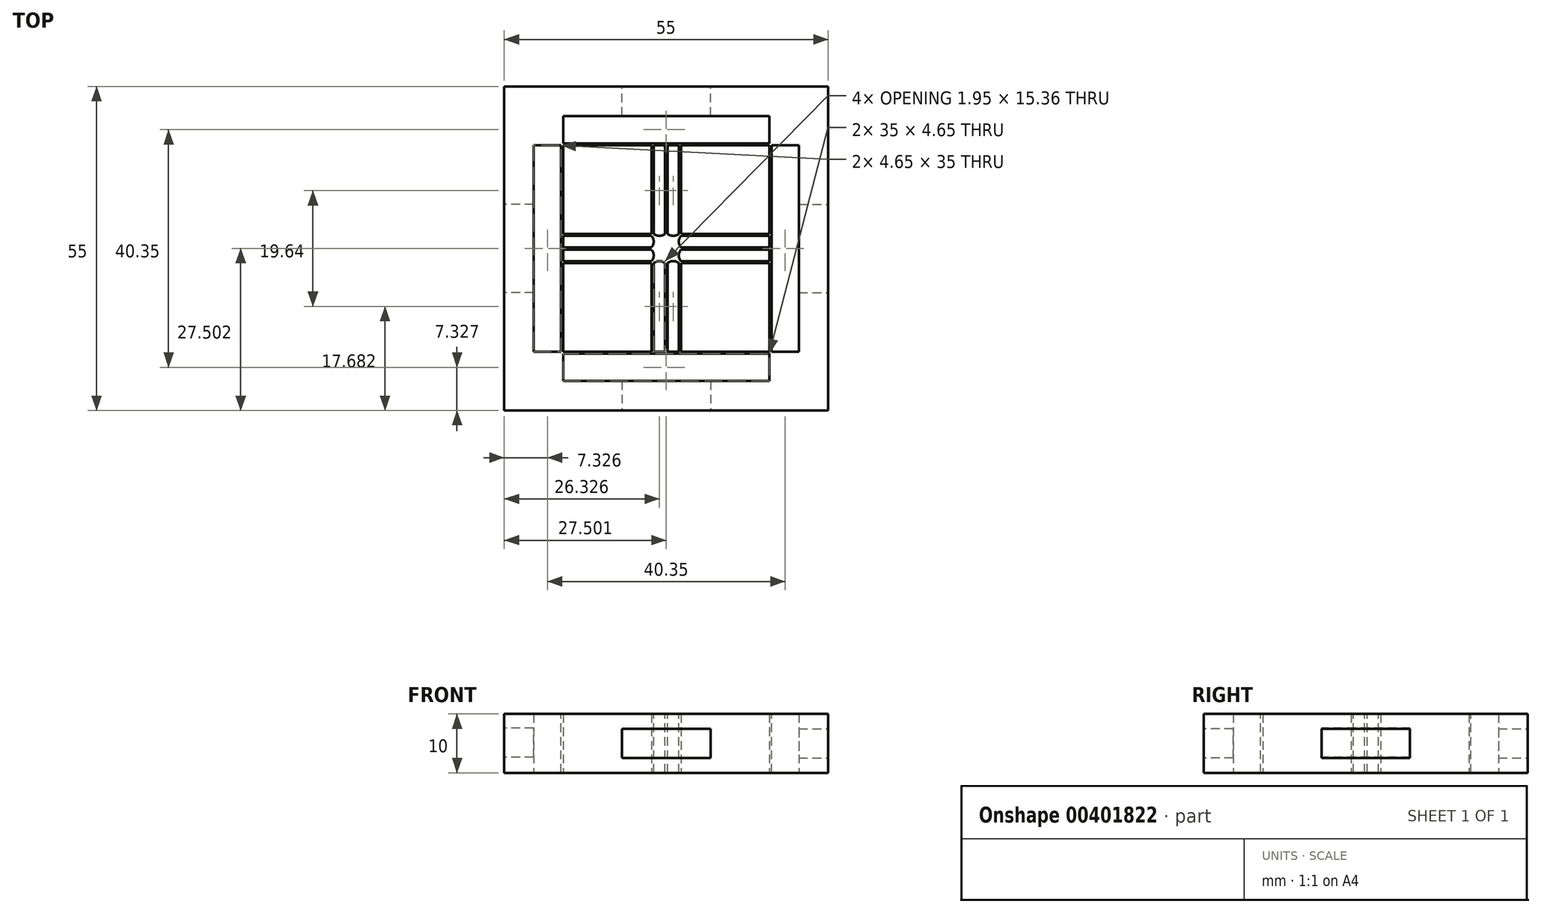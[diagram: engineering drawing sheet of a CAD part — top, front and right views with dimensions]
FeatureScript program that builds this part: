
annotation { "Feature Type Name" : "Feature", "Feature Type Description" : "" }
export const myFeature = defineFeature(function(context is Context, id is Id, definition is map)
    precondition{}
    {
        {
            var Q0;
            Q0=qCreatedBy(makeId("Top.planeOp"),FACE);
            var sketch = newSketch(context, id + "F0", { "sketchPlane" : qUnion([Q0])});
            skLineSegment(sketch, "E0.bottom", {"start": v(-73.72, 37.36) * mm, "end": v(-18.72, 37.36) * mm});
            skLineSegment(sketch, "E0.top", {"start": v(-73.72, -17.64) * mm, "end": v(-18.72, -17.64) * mm});
            skLineSegment(sketch, "E0.left", {"start": v(-73.72, 37.36) * mm, "end": v(-73.72, -17.64) * mm});
            skLineSegment(sketch, "E0.right", {"start": v(-18.72, 37.36) * mm, "end": v(-18.72, -17.64) * mm});
            skSolve(sketch);
        }
        {
            var Q0;
            Q0=makeQuery(id+"F0.imprint","IMPRINT",FACE,{"disambiguationData":[TD([[makeQuery(id+"F0.imprint","IMPRINT",EDGE,{"derivedFrom":sQuery(id+"F0.wireOp",EDGE,"E0.bottom")}),-1.0]])]});
            var sketch = newSketch(context, id + "F1", { "sketchPlane" : qUnion([Q0])});
            skLineSegment(sketch, "E1.bottom", {"start": v(-63.72, 32.36) * mm, "end": v(-28.72, 32.36) * mm});
            skLineSegment(sketch, "E1.top", {"start": v(-63.72, 28.36) * mm, "end": v(-28.72, 28.36) * mm});
            skLineSegment(sketch, "E1.left", {"start": v(-63.72, 32.36) * mm, "end": v(-63.72, 28.36) * mm});
            skLineSegment(sketch, "E1.right", {"start": v(-28.72, 32.36) * mm, "end": v(-28.72, 28.36) * mm});
            skLineSegment(sketch, "E2.bottom", {"start": v(-64.72, 27.36) * mm, "end": v(-68.72, 27.36) * mm});
            skLineSegment(sketch, "E2.top", {"start": v(-64.72, -7.64) * mm, "end": v(-68.72, -7.64) * mm});
            skLineSegment(sketch, "E2.left", {"start": v(-64.72, 27.36) * mm, "end": v(-64.72, -7.64) * mm});
            skLineSegment(sketch, "E2.right", {"start": v(-68.72, 27.36) * mm, "end": v(-68.72, -7.64) * mm});
            skLineSegment(sketch, "E3.bottom", {"start": v(-23.72, 27.36) * mm, "end": v(-27.72, 27.36) * mm});
            skLineSegment(sketch, "E3.top", {"start": v(-23.72, -7.64) * mm, "end": v(-27.72, -7.64) * mm});
            skLineSegment(sketch, "E3.left", {"start": v(-23.72, 27.36) * mm, "end": v(-23.72, -7.64) * mm});
            skLineSegment(sketch, "E3.right", {"start": v(-27.72, 27.36) * mm, "end": v(-27.72, -7.64) * mm});
            skLineSegment(sketch, "E4.bottom", {"start": v(-63.72, -8.64) * mm, "end": v(-28.72, -8.64) * mm});
            skLineSegment(sketch, "E4.top", {"start": v(-63.72, -12.64) * mm, "end": v(-28.72, -12.64) * mm});
            skLineSegment(sketch, "E4.left", {"start": v(-63.72, -8.64) * mm, "end": v(-63.72, -12.64) * mm});
            skLineSegment(sketch, "E4.right", {"start": v(-28.72, -8.64) * mm, "end": v(-28.72, -12.64) * mm});
            skLineSegment(sketch, "E5.bottom", {"start": v(-63.72, 27.36) * mm, "end": v(-48.72, 27.36) * mm});
            skLineSegment(sketch, "E5.top", {"start": v(-63.72, 12.36) * mm, "end": v(-48.72, 12.36) * mm});
            skLineSegment(sketch, "E5.left", {"start": v(-63.72, 27.36) * mm, "end": v(-63.72, 12.36) * mm});
            skLineSegment(sketch, "E5.right", {"start": v(-48.72, 27.36) * mm, "end": v(-48.72, 12.36) * mm});
            skLineSegment(sketch, "E6.bottom", {"start": v(-43.72, 27.36) * mm, "end": v(-28.72, 27.36) * mm});
            skLineSegment(sketch, "E6.top", {"start": v(-43.72, 12.36) * mm, "end": v(-28.72, 12.36) * mm});
            skLineSegment(sketch, "E6.left", {"start": v(-43.72, 27.36) * mm, "end": v(-43.72, 12.36) * mm});
            skLineSegment(sketch, "E6.right", {"start": v(-28.72, 27.36) * mm, "end": v(-28.72, 12.36) * mm});
            skLineSegment(sketch, "E7.bottom", {"start": v(-63.72, 7.36) * mm, "end": v(-48.72, 7.36) * mm});
            skLineSegment(sketch, "E7.top", {"start": v(-63.72, -7.64) * mm, "end": v(-48.72, -7.64) * mm});
            skLineSegment(sketch, "E7.left", {"start": v(-63.72, 7.36) * mm, "end": v(-63.72, -7.64) * mm});
            skLineSegment(sketch, "E7.right", {"start": v(-48.72, 7.36) * mm, "end": v(-48.72, -7.64) * mm});
            skLineSegment(sketch, "E8.bottom", {"start": v(-43.72, 7.36) * mm, "end": v(-28.72, 7.36) * mm});
            skLineSegment(sketch, "E8.top", {"start": v(-43.72, -7.64) * mm, "end": v(-28.72, -7.64) * mm});
            skLineSegment(sketch, "E8.left", {"start": v(-43.72, 7.36) * mm, "end": v(-43.72, -7.64) * mm});
            skLineSegment(sketch, "E8.right", {"start": v(-28.72, 7.36) * mm, "end": v(-28.72, -7.64) * mm});
            skSolve(sketch);
        }
        {
            var Q0;
            Q0 = qSketchRegion(id + "F0", true);
            extrude(context, id + "F2", {"entities" : qUnion([Q0]), "depth" : 10 * mm});
        }
        {
            var Q0;
            Q0 = qSketchRegion(id + "F1", true);
            extrude(context, id + "F3", {"entities" : qUnion([Q0]), "operationType" : NewBodyOperationType.REMOVE, "depth" : 25 * mm});
        }
        {
            var Q0;
            Q0=makeQuery(id+"F2.opExtrude","CAP_FACE",FACE,{"disambiguationData":[OSD([sQuery(id+"F0.wireOp",EDGE,"E0.bottom"),sQuery(id+"F0.wireOp",EDGE,"E0.top"),sQuery(id+"F0.wireOp",EDGE,"E0.left"),sQuery(id+"F0.wireOp",EDGE,"E0.right")])],"isStart":false});
            var sketch = newSketch(context, id + "F4", { "sketchPlane" : qUnion([Q0])});
            skLineSegment(sketch, "E9.bottom", {"start": v(-48.37, 27.36) * mm, "end": v(-46.42, 27.36) * mm});
            skLineSegment(sketch, "E9.top", {"start": v(-48.37, 12.36) * mm, "end": v(-46.42, 12.36) * mm});
            skLineSegment(sketch, "E9.left", {"start": v(-48.37, 27.36) * mm, "end": v(-48.37, 12.36) * mm});
            skLineSegment(sketch, "E9.right", {"start": v(-46.42, 27.36) * mm, "end": v(-46.42, 12.36) * mm});
            skSolve(sketch);
        }
        {
            var Q0;
            Q0 = qSketchRegion(id + "F4", true);
            extrude(context, id + "F5", {"entities" : qUnion([Q0]), "operationType" : NewBodyOperationType.REMOVE, "oppositeDirection" : true, "depth" : 25 * mm});
        }
        {
            var Q0;
            Q0=makeQuery(id+"F2.opExtrude","CAP_FACE",FACE,{"disambiguationData":[OSD([sQuery(id+"F0.wireOp",EDGE,"E0.bottom"),sQuery(id+"F0.wireOp",EDGE,"E0.top"),sQuery(id+"F0.wireOp",EDGE,"E0.left"),sQuery(id+"F0.wireOp",EDGE,"E0.right")])],"isStart":false});
            var sketch = newSketch(context, id + "F6", { "sketchPlane" : qUnion([Q0])});
            skLineSegment(sketch, "E10.bottom", {"start": v(-46.02, 12.36) * mm, "end": v(-44.07, 12.36) * mm});
            skLineSegment(sketch, "E10.top", {"start": v(-46.02, 27.36) * mm, "end": v(-44.07, 27.36) * mm});
            skLineSegment(sketch, "E10.left", {"start": v(-46.02, 12.36) * mm, "end": v(-46.02, 27.36) * mm});
            skLineSegment(sketch, "E10.right", {"start": v(-44.07, 12.36) * mm, "end": v(-44.07, 27.36) * mm});
            skSolve(sketch);
        }
        {
            var Q0;
            Q0 = qSketchRegion(id + "F6", true);
            extrude(context, id + "F7", {"entities" : qUnion([Q0]), "operationType" : NewBodyOperationType.REMOVE, "oppositeDirection" : true, "depth" : 25 * mm});
        }
        {
            var Q0;
            Q0=makeQuery(id+"F2.opExtrude","CAP_FACE",FACE,{"disambiguationData":[OSD([sQuery(id+"F0.wireOp",EDGE,"E0.bottom"),sQuery(id+"F0.wireOp",EDGE,"E0.top"),sQuery(id+"F0.wireOp",EDGE,"E0.left"),sQuery(id+"F0.wireOp",EDGE,"E0.right")])],"isStart":false});
            var sketch = newSketch(context, id + "F8", { "sketchPlane" : qUnion([Q0])});
            skLineSegment(sketch, "E11.bottom", {"start": v(-48.72, 12.01) * mm, "end": v(-63.72, 12.01) * mm});
            skLineSegment(sketch, "E11.top", {"start": v(-48.72, 10.06) * mm, "end": v(-63.72, 10.06) * mm});
            skLineSegment(sketch, "E11.left", {"start": v(-48.72, 12.01) * mm, "end": v(-48.72, 10.06) * mm});
            skLineSegment(sketch, "E11.right", {"start": v(-63.72, 12.01) * mm, "end": v(-63.72, 10.06) * mm});
            skLineSegment(sketch, "E12.bottom", {"start": v(-48.72, 9.66) * mm, "end": v(-63.72, 9.66) * mm});
            skLineSegment(sketch, "E12.top", {"start": v(-48.72, 7.71) * mm, "end": v(-63.72, 7.71) * mm});
            skLineSegment(sketch, "E12.left", {"start": v(-48.72, 9.66) * mm, "end": v(-48.72, 7.71) * mm});
            skLineSegment(sketch, "E12.right", {"start": v(-63.72, 9.66) * mm, "end": v(-63.72, 7.71) * mm});
            skLineSegment(sketch, "E13.bottom", {"start": v(-43.72, 12.01) * mm, "end": v(-28.72, 12.01) * mm});
            skLineSegment(sketch, "E13.top", {"start": v(-43.72, 10.06) * mm, "end": v(-28.72, 10.06) * mm});
            skLineSegment(sketch, "E13.left", {"start": v(-43.72, 12.01) * mm, "end": v(-43.72, 10.06) * mm});
            skLineSegment(sketch, "E13.right", {"start": v(-28.72, 12.01) * mm, "end": v(-28.72, 10.06) * mm});
            skLineSegment(sketch, "E14.bottom", {"start": v(-43.72, 9.66) * mm, "end": v(-28.72, 9.66) * mm});
            skLineSegment(sketch, "E14.top", {"start": v(-43.72, 7.71) * mm, "end": v(-28.72, 7.71) * mm});
            skLineSegment(sketch, "E14.left", {"start": v(-43.72, 9.66) * mm, "end": v(-43.72, 7.71) * mm});
            skLineSegment(sketch, "E14.right", {"start": v(-28.72, 9.66) * mm, "end": v(-28.72, 7.71) * mm});
            skLineSegment(sketch, "E15.bottom", {"start": v(-48.37, 7.36) * mm, "end": v(-46.42, 7.36) * mm});
            skLineSegment(sketch, "E15.top", {"start": v(-48.37, -7.64) * mm, "end": v(-46.42, -7.64) * mm});
            skLineSegment(sketch, "E15.left", {"start": v(-48.37, 7.36) * mm, "end": v(-48.37, -7.64) * mm});
            skLineSegment(sketch, "E15.right", {"start": v(-46.42, 7.36) * mm, "end": v(-46.42, -7.64) * mm});
            skLineSegment(sketch, "E16.bottom", {"start": v(-46.02, 7.36) * mm, "end": v(-44.07, 7.36) * mm});
            skLineSegment(sketch, "E16.top", {"start": v(-46.02, -7.64) * mm, "end": v(-44.07, -7.64) * mm});
            skLineSegment(sketch, "E16.left", {"start": v(-46.02, 7.36) * mm, "end": v(-46.02, -7.64) * mm});
            skLineSegment(sketch, "E16.right", {"start": v(-44.07, 7.36) * mm, "end": v(-44.07, -7.64) * mm});
            skSolve(sketch);
        }
        {
            var Q0;
            Q0 = qSketchRegion(id + "F8", true);
            extrude(context, id + "F9", {"entities" : qUnion([Q0]), "operationType" : NewBodyOperationType.REMOVE, "oppositeDirection" : true, "depth" : 25 * mm});
        }
        {
            var Q0;
            Q0=makeQuery(id+"F2.opExtrude","CAP_FACE",FACE,{"disambiguationData":[OSD([sQuery(id+"F0.wireOp",EDGE,"E0.bottom"),sQuery(id+"F0.wireOp",EDGE,"E0.top"),sQuery(id+"F0.wireOp",EDGE,"E0.left"),sQuery(id+"F0.wireOp",EDGE,"E0.right")])],"isStart":false});
            var sketch = newSketch(context, id + "F10", { "sketchPlane" : qUnion([Q0])});
            skLineSegment(sketch, "E17.bottom", {"start": v(-63.72, 32.36) * mm, "end": v(-28.72, 32.36) * mm});
            skLineSegment(sketch, "E17.top", {"start": v(-63.72, 27.71) * mm, "end": v(-28.72, 27.71) * mm});
            skLineSegment(sketch, "E17.left", {"start": v(-63.72, 32.36) * mm, "end": v(-63.72, 27.71) * mm});
            skLineSegment(sketch, "E17.right", {"start": v(-28.72, 32.36) * mm, "end": v(-28.72, 27.71) * mm});
            skLineSegment(sketch, "E18.bottom", {"start": v(-23.72, 27.36) * mm, "end": v(-28.37, 27.36) * mm});
            skLineSegment(sketch, "E18.top", {"start": v(-23.72, -7.64) * mm, "end": v(-28.37, -7.64) * mm});
            skLineSegment(sketch, "E18.left", {"start": v(-23.72, 27.36) * mm, "end": v(-23.72, -7.64) * mm});
            skLineSegment(sketch, "E18.right", {"start": v(-28.37, 27.36) * mm, "end": v(-28.37, -7.64) * mm});
            skLineSegment(sketch, "E19.bottom", {"start": v(-28.72, -12.64) * mm, "end": v(-63.72, -12.64) * mm});
            skLineSegment(sketch, "E19.top", {"start": v(-28.72, -7.99) * mm, "end": v(-63.72, -7.99) * mm});
            skLineSegment(sketch, "E19.left", {"start": v(-28.72, -12.64) * mm, "end": v(-28.72, -7.99) * mm});
            skLineSegment(sketch, "E19.right", {"start": v(-63.72, -12.64) * mm, "end": v(-63.72, -7.99) * mm});
            skLineSegment(sketch, "E20.bottom", {"start": v(-68.72, -7.64) * mm, "end": v(-64.07, -7.64) * mm});
            skLineSegment(sketch, "E20.top", {"start": v(-68.72, 27.36) * mm, "end": v(-64.07, 27.36) * mm});
            skLineSegment(sketch, "E20.left", {"start": v(-68.72, -7.64) * mm, "end": v(-68.72, 27.36) * mm});
            skLineSegment(sketch, "E20.right", {"start": v(-64.07, -7.64) * mm, "end": v(-64.07, 27.36) * mm});
            skSolve(sketch);
        }
        {
            var Q0;
            Q0 = qSketchRegion(id + "F10", true);
            extrude(context, id + "F11", {"entities" : qUnion([Q0]), "operationType" : NewBodyOperationType.REMOVE, "oppositeDirection" : true, "depth" : 25 * mm});
        }
        {
            var Q0;
            Q0=makeQuery(id+"F2.opExtrude","CAP_FACE",FACE,{"disambiguationData":[OSD([sQuery(id+"F0.wireOp",EDGE,"E0.bottom"),sQuery(id+"F0.wireOp",EDGE,"E0.top"),sQuery(id+"F0.wireOp",EDGE,"E0.left"),sQuery(id+"F0.wireOp",EDGE,"E0.right")])],"isStart":false});
            var sketch = newSketch(context, id + "F12", { "sketchPlane" : qUnion([Q0])});
            skArc(sketch, "E21", {"start": v(-48.37, 12.36) * mm, "mid": v(-47.4, 12) * mm, "end": v(-46.42, 12.36) * mm});
            skArc(sketch, "E22", {"start": v(-46.02, 12.36) * mm, "mid": v(-45.04, 12) * mm, "end": v(-44.07, 12.36) * mm});
            skPoint(sketch, "E22.midSnap0", {"position": v(-45.04, 12.36) * mm});
            skPoint(sketch, "E22.midSnap1", {"position": v(-47.4, 12) * mm});
            skArc(sketch, "E23", {"start": v(-43.72, 12.01) * mm, "mid": v(-44.08, 11.04) * mm, "end": v(-43.72, 10.06) * mm});
            skArc(sketch, "E24", {"start": v(-43.72, 9.66) * mm, "mid": v(-44.08, 8.69) * mm, "end": v(-43.72, 7.71) * mm});
            skArc(sketch, "E25", {"start": v(-44.07, 7.36) * mm, "mid": v(-45.04, 7.72) * mm, "end": v(-46.02, 7.36) * mm});
            skArc(sketch, "E26", {"start": v(-46.42, 7.36) * mm, "mid": v(-47.4, 7.72) * mm, "end": v(-48.37, 7.36) * mm});
            skArc(sketch, "E27", {"start": v(-48.72, 7.71) * mm, "mid": v(-48.36, 8.69) * mm, "end": v(-48.72, 9.66) * mm});
            skArc(sketch, "E28", {"start": v(-48.72, 10.06) * mm, "mid": v(-48.36, 11.04) * mm, "end": v(-48.72, 12.01) * mm});
            skLineSegment(sketch, "E29", {"start": v(-48.37, 12.36) * mm, "end": v(-46.42, 12.36) * mm});
            skLineSegment(sketch, "E30", {"start": v(-46.02, 12.36) * mm, "end": v(-44.07, 12.36) * mm});
            skLineSegment(sketch, "E31", {"start": v(-48.72, 10.06) * mm, "end": v(-48.72, 12.01) * mm});
            skLineSegment(sketch, "E32", {"start": v(-48.72, 9.66) * mm, "end": v(-48.72, 7.71) * mm});
            skLineSegment(sketch, "E33", {"start": v(-48.37, 7.36) * mm, "end": v(-46.42, 7.36) * mm});
            skLineSegment(sketch, "E34", {"start": v(-46.02, 7.36) * mm, "end": v(-44.07, 7.36) * mm});
            skLineSegment(sketch, "E35", {"start": v(-43.72, 7.71) * mm, "end": v(-43.72, 9.66) * mm});
            skLineSegment(sketch, "E36", {"start": v(-43.72, 10.06) * mm, "end": v(-43.72, 12.01) * mm});
            skSolve(sketch);
        }
        {
            var Q0;
            Q0 = qSketchRegion(id + "F12", true);
            extrude(context, id + "F13", {"entities" : qUnion([Q0]), "operationType" : NewBodyOperationType.REMOVE, "oppositeDirection" : true, "depth" : 25 * mm});
        }
        {
            var Q0;
            Q0=makeQuery(id+"F2.opExtrude","SWEPT_FACE",FACE,{"disambiguationData":[OSD([sQuery(id+"F0.wireOp",EDGE,"E0.top")])]});
            var sketch = newSketch(context, id + "F14", { "sketchPlane" : qUnion([Q0])});
            skLineSegment(sketch, "E37.bottom", {"start": v(-53.72, 7.5) * mm, "end": v(-38.72, 7.5) * mm});
            skLineSegment(sketch, "E37.top", {"start": v(-53.72, 2.5) * mm, "end": v(-38.72, 2.5) * mm});
            skLineSegment(sketch, "E37.left", {"start": v(-53.72, 7.5) * mm, "end": v(-53.72, 2.5) * mm});
            skLineSegment(sketch, "E37.right", {"start": v(-38.72, 7.5) * mm, "end": v(-38.72, 2.5) * mm});
            skSolve(sketch);
        }
        {
            var Q0;
            Q0 = qSketchRegion(id + "F14", true);
            extrude(context, id + "F15", {"entities" : qUnion([Q0]), "operationType" : NewBodyOperationType.REMOVE, "oppositeDirection" : true, "depth" : 6 * mm});
        }
        {
            var Q0;
            Q0=makeQuery(id+"F2.opExtrude","SWEPT_FACE",FACE,{"disambiguationData":[OSD([sQuery(id+"F0.wireOp",EDGE,"E0.right")])]});
            var sketch = newSketch(context, id + "F16", { "sketchPlane" : qUnion([Q0])});
            skLineSegment(sketch, "E38.bottom", {"start": v(2.36, 7.5) * mm, "end": v(17.36, 7.5) * mm});
            skLineSegment(sketch, "E38.top", {"start": v(2.36, 2.5) * mm, "end": v(17.36, 2.5) * mm});
            skLineSegment(sketch, "E38.left", {"start": v(2.36, 7.5) * mm, "end": v(2.36, 2.5) * mm});
            skLineSegment(sketch, "E38.right", {"start": v(17.36, 7.5) * mm, "end": v(17.36, 2.5) * mm});
            skSolve(sketch);
        }
        {
            var Q0;
            Q0 = qSketchRegion(id + "F16", true);
            extrude(context, id + "F17", {"entities" : qUnion([Q0]), "operationType" : NewBodyOperationType.REMOVE, "oppositeDirection" : true, "depth" : 6 * mm});
        }
        {
            var Q0;
            Q0=makeQuery(id+"F2.opExtrude","SWEPT_FACE",FACE,{"disambiguationData":[OSD([sQuery(id+"F0.wireOp",EDGE,"E0.bottom")])]});
            var sketch = newSketch(context, id + "F18", { "sketchPlane" : qUnion([Q0])});
            skLineSegment(sketch, "E39.bottom", {"start": v(38.72, 7.5) * mm, "end": v(53.72, 7.5) * mm});
            skLineSegment(sketch, "E39.top", {"start": v(38.72, 2.5) * mm, "end": v(53.72, 2.5) * mm});
            skLineSegment(sketch, "E39.left", {"start": v(38.72, 7.5) * mm, "end": v(38.72, 2.5) * mm});
            skLineSegment(sketch, "E39.right", {"start": v(53.72, 7.5) * mm, "end": v(53.72, 2.5) * mm});
            skSolve(sketch);
        }
        {
            var Q0;
            Q0 = qSketchRegion(id + "F18", true);
            extrude(context, id + "F19", {"entities" : qUnion([Q0]), "operationType" : NewBodyOperationType.REMOVE, "oppositeDirection" : true, "depth" : 6 * mm});
        }
        {
            var Q0;
            Q0=makeQuery(id+"F2.opExtrude","SWEPT_FACE",FACE,{"disambiguationData":[OSD([sQuery(id+"F0.wireOp",EDGE,"E0.left")])]});
            var sketch = newSketch(context, id + "F20", { "sketchPlane" : qUnion([Q0])});
            skLineSegment(sketch, "E40.bottom", {"start": v(-17.36, 7.62) * mm, "end": v(-2.36, 7.62) * mm});
            skLineSegment(sketch, "E40.top", {"start": v(-17.36, 2.62) * mm, "end": v(-2.36, 2.62) * mm});
            skLineSegment(sketch, "E40.left", {"start": v(-17.36, 7.62) * mm, "end": v(-17.36, 2.62) * mm});
            skLineSegment(sketch, "E40.right", {"start": v(-2.36, 7.62) * mm, "end": v(-2.36, 2.62) * mm});
            skSolve(sketch);
        }
        {
            var Q0;
            Q0 = qSketchRegion(id + "F20", true);
            extrude(context, id + "F21", {"entities" : qUnion([Q0]), "operationType" : NewBodyOperationType.REMOVE, "oppositeDirection" : true, "depth" : 6 * mm});
        }
    });
